# Revit family: Bath&ShowerMixer-(Built-in,Exposedpart)-Vitra-MinimaxSSeries-A42210
name_source: partatom
category: Plumbing Fixtures
revit_build: Autodesk Revit 2017 (Build: 20160225_1515(x64)
units: mm (PartAtom-declared; Revit-internal decimal feet)

## family parameters
Cut with Voids When Loaded = No
Host = Face
OmniClass Number = 23.45.55.17
OmniClass Title = Mixing Faucets
Part Type = Normal
Room Calculation Point = No
Round Connector Dimension = Use Diameter
Shared = Yes

## types (7) — shared parameters
BIMobject category = Bath/Shower Mixer
CW Connection = Yes
Default Elevation = 850 mm  [stored 2.78871 ft]
Depth(mm) = 204 mm
Description = Bath&ShowerMixer-(Built-in,Exposedpart)-Vitra-MinimaxSSeries
Design country = Turkey
HW Connection = Yes
Height(mm) = 114 mm  [stored 0.374016 ft]
Hot Water Supply (max.) = 80 °C
Hot Water temperature, factory set to = 38 °C
IFC Classification = Sanitary Terminal
Main Material = Brass
Manufacturer = Vitra
Manufacturer name = Vitra
Masterformat 2014 Code = 22 40 00
Masterformat 2014 Description = Plumbing Fixtures
Min. flow pressure of = 0.5 bar
MountingType = Wall-mounted (exposed part)
NBS Referans Code = 45-35-70/315
NBS Referans Description = Water supply fittings for baths
Nominal height = 0.000
Nominal width = 0.000
OmniClass Code = 23.45.55.17
OmniClass Description = Mixing Faucets
Product Guid = https://cdn.vitra.com.tr
Product Type = Built-in bath/shower mixer (exposed part)
Product certification = https://vitraglobal.com
Product data url = https://www.vitraglobal.com
Product family = Minimax S
Product group = Bath&Shower Mixer (exposed part)
Range of Hot Water Supply = 5 - 65 °C
Range of flow pressure = 1 - 5 bar
Technical description = https://www.vitraglobal.com
Test Pressure = 16 bar
UNSPSC Code = 301815
URL = https://vitraglobal.com
Uniclass 1.4 Code = L725111
Uniclass 1.4 Description = Mixer taps
Uniclass 2.0 Code = Pr_40_20_87_09
Uniclass 2.0 Description = Bath taps
Uniclass 2015 Code = Pr_40_20_87_09
Uniclass 2015 Name = Bath taps
Uniformat II Code = 22 40 00
Uniformat II Description = Plumbing Fixture
Weight Net (kg) = 0,590
Width(mm) = 170 mm  [stored 0.557743 ft]
Youtube = https://www.youtube.com
zero-valued in all types: CWFU, Connection Diameter (mm), Cost, HWFU, Number Of Connections, WFU

## per-type parameters (varying)
| type | Article No. (default) | Brand | Coating Material | Color | Model | Product SKU | Warranty Period (Year) |
| Built-inBath&ShowerMixer(Exposedpart)-Vitra-MinimaxSSeries-A42210 | A42210 | Artema | Chrome | Chrome | A42210 | A42210 | 10 Years |
| Built-inBath&ShowerMixer(Exposedpart)-Vitra-MinimaxSSeries-A4221036 | A4221036 | Vitra | Black | Black | A4221036 | A4221036 | 7 Years |
| Built-inBath&ShowerMixer(Exposedpart)-Vitra-MinimaxSSeries-A42210ENR | A42210ENR | Artema | Chrome | Chrome | A42210ENR | A42210ENR | 10 Years |
| Built-inBath&ShowerMixer(Exposedpart)-Vitra-MinimaxSSeries-A42210EXP | A42210EXP | Vitra | Chrome | Chrome | A42210EXP | A42210EXP | 7 Years |
| Built-inBath&ShowerMixer(Exposedpart)-Vitra-MinimaxSSeries-A42210INV | A42210INV | Vitra | Chrome | Chrome | A42210INV | A42210INV | 7 Years |
| Built-inBath&ShowerMixer(Exposedpart)-Vitra-MinimaxSSeries-A42210TPX | A42210TPX | Vitra | Chrome | Chrome | A42210TPX | A42210TPX | 7 Years |
| Built-inBath&ShowerMixer(Exposedpart)-Vitra-MinimaxSSeries-A42210VUK | A42210VUK | Vitra | Chrome | Chrome | A42210VUK | A42210VUK | 7 Years |

note: [stored X ft] marks values corroborated as IEEE doubles in the binary element streams (Revit-internal decimal feet)

## geometry (parser evidence)
native form markers: Sweep x3
no freeform markers — native parametric forms only
